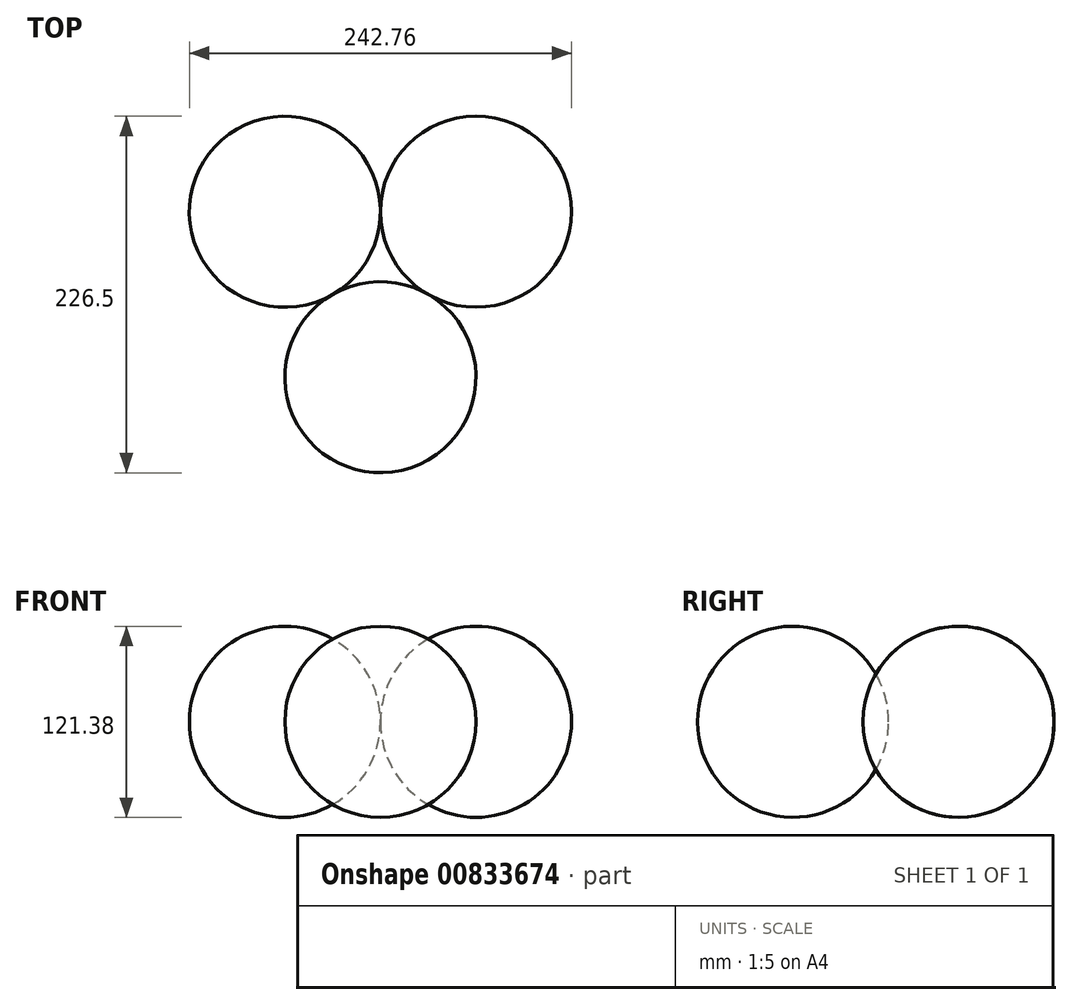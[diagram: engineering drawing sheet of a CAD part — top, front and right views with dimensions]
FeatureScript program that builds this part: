
annotation { "Feature Type Name" : "Feature", "Feature Type Description" : "" }
export const myFeature = defineFeature(function(context is Context, id is Id, definition is map)
    precondition{}
    {
        {
            var Q0;
            Q0=qCreatedBy(makeId("Top.planeOp"),FACE);
            var sketch = newSketch(context, id + "F0", { "sketchPlane" : qUnion([Q0])});
            skCircle(sketch, "E0.cCircle", {"center": v(0, 0) * mm, "radius": 35.04 * mm, "construction": true});
            skLineSegment(sketch, "E0.0", {"start": v(-60.7, 35.04) * mm, "end": v(60.7, 35.04) * mm});
            skLineSegment(sketch, "E0.1", {"start": v(60.7, 35.04) * mm, "end": v(0, -70.08) * mm});
            skLineSegment(sketch, "E0.2", {"start": v(0, -70.08) * mm, "end": v(-60.7, 35.04) * mm});
            skPoint(sketch, "E0.0.midPoint", {"position": v(0, 35.04) * mm});
            skCircle(sketch, "E1", {"center": v(-60.7, 35.04) * mm, "radius": 60.7 * mm});
            skCircle(sketch, "E2", {"center": v(60.7, 35.04) * mm, "radius": 60.7 * mm});
            skCircle(sketch, "E3", {"center": v(0, -70.08) * mm, "radius": 60.7 * mm});
            skLineSegment(sketch, "E4", {"start": v(-30.35, -17.52) * mm, "end": v(-104.39, 110.72) * mm});
            skLineSegment(sketch, "E5", {"start": v(-30.35, -17.52) * mm, "end": v(46.47, -150.56) * mm});
            skLineSegment(sketch, "E6", {"start": v(0, 35.04) * mm, "end": v(150.38, 35.04) * mm});
            skSolve(sketch);
        }
        {
            var Q0;
            {var subQ0=sQuery(id+"F0.wireOp",EDGE,"E5");var subQ4=makeQuery(id+"F0.imprint","INTERSECT",VERTEX,{"derivedFrom":[sQuery(id+"F0.wireOp",EDGE,"E0.1"),subQ0]});Q0=makeQuery(id+"F0.imprint","IMPRINT",FACE,{"disambiguationData":[TD([[makeQuery(id+"F0.imprint","IMPRINT",EDGE,{"disambiguationData":[TD([[subQ4,-1.0]])],"derivedFrom":subQ0}),-1.0]])]});}
            var Q1;
            Q1=sQuery(id+"F0.wireOp",EDGE,"E5");
            revolve(context, id + "F1", {"surfaceOperationType" : NewSurfaceOperationType.NEW, "entities" : qUnion([Q0]), "axis" : qUnion([Q1]), "revolveType" : RevolveType.FULL});
        }
        {
            var Q0;
            {var subQ0=sQuery(id+"F0.wireOp",EDGE,"E6");var subQ4=makeQuery(id+"F0.imprint","INTERSECT",VERTEX,{"derivedFrom":[sQuery(id+"F0.wireOp",EDGE,"E0.1"),subQ0]});Q0=makeQuery(id+"F0.imprint","IMPRINT",FACE,{"disambiguationData":[TD([[makeQuery(id+"F0.imprint","IMPRINT",EDGE,{"disambiguationData":[TD([[subQ4,-1.0]])],"derivedFrom":subQ0}),1.0]])]});}
            var Q1;
            Q1=sQuery(id+"F0.wireOp",EDGE,"E6");
            revolve(context, id + "F2", {"surfaceOperationType" : NewSurfaceOperationType.NEW, "entities" : qUnion([Q0]), "axis" : qUnion([Q1]), "revolveType" : RevolveType.FULL});
        }
        {
            var Q0;
            {var subQ0=sQuery(id+"F0.wireOp",EDGE,"E4");var subQ4=makeQuery(id+"F0.imprint","INTERSECT",VERTEX,{"derivedFrom":[sQuery(id+"F0.wireOp",EDGE,"E0.0"),subQ0]});Q0=makeQuery(id+"F0.imprint","IMPRINT",FACE,{"disambiguationData":[TD([[makeQuery(id+"F0.imprint","IMPRINT",EDGE,{"disambiguationData":[TD([[subQ4,-1.0]])],"derivedFrom":subQ0}),1.0]])]});}
            var Q1;
            Q1=sQuery(id+"F0.wireOp",EDGE,"E4");
            revolve(context, id + "F3", {"surfaceOperationType" : NewSurfaceOperationType.NEW, "entities" : qUnion([Q0]), "axis" : qUnion([Q1]), "revolveType" : RevolveType.FULL});
        }
    });
